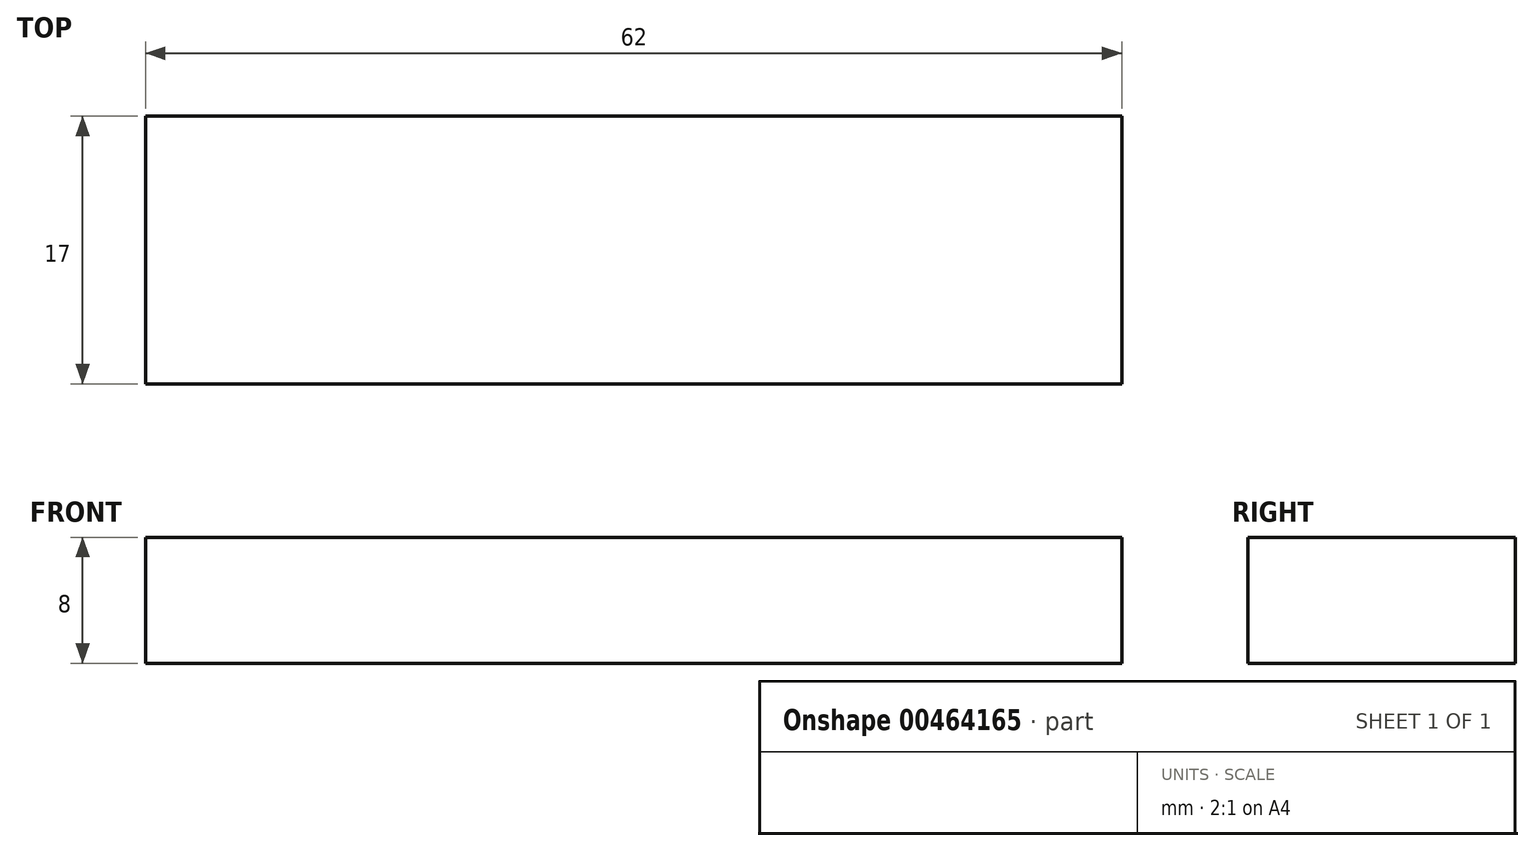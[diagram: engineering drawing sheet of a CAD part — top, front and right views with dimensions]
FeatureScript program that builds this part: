
annotation { "Feature Type Name" : "Feature", "Feature Type Description" : "" }
export const myFeature = defineFeature(function(context is Context, id is Id, definition is map)
    precondition{}
    {
        {
            var Q0;
            Q0=qCreatedBy(makeId("Top.planeOp"),FACE);
            var sketch = newSketch(context, id + "F0", { "sketchPlane" : qUnion([Q0])});
            skLineSegment(sketch, "E0.bottom", {"start": v(-64.05, -0.16) * mm, "end": v(-2.05, -0.16) * mm});
            skLineSegment(sketch, "E0.top", {"start": v(-64.05, -17.16) * mm, "end": v(-2.05, -17.16) * mm});
            skLineSegment(sketch, "E0.left", {"start": v(-64.05, -0.16) * mm, "end": v(-64.05, -17.16) * mm});
            skLineSegment(sketch, "E0.right", {"start": v(-2.05, -0.16) * mm, "end": v(-2.05, -17.16) * mm});
            skSolve(sketch);
        }
        {
            var Q0;
            Q0 = qSketchRegion(id + "F0", true);
            extrude(context, id + "F1", {"entities" : qUnion([Q0]), "depth" : 8 * mm});
        }
    });
